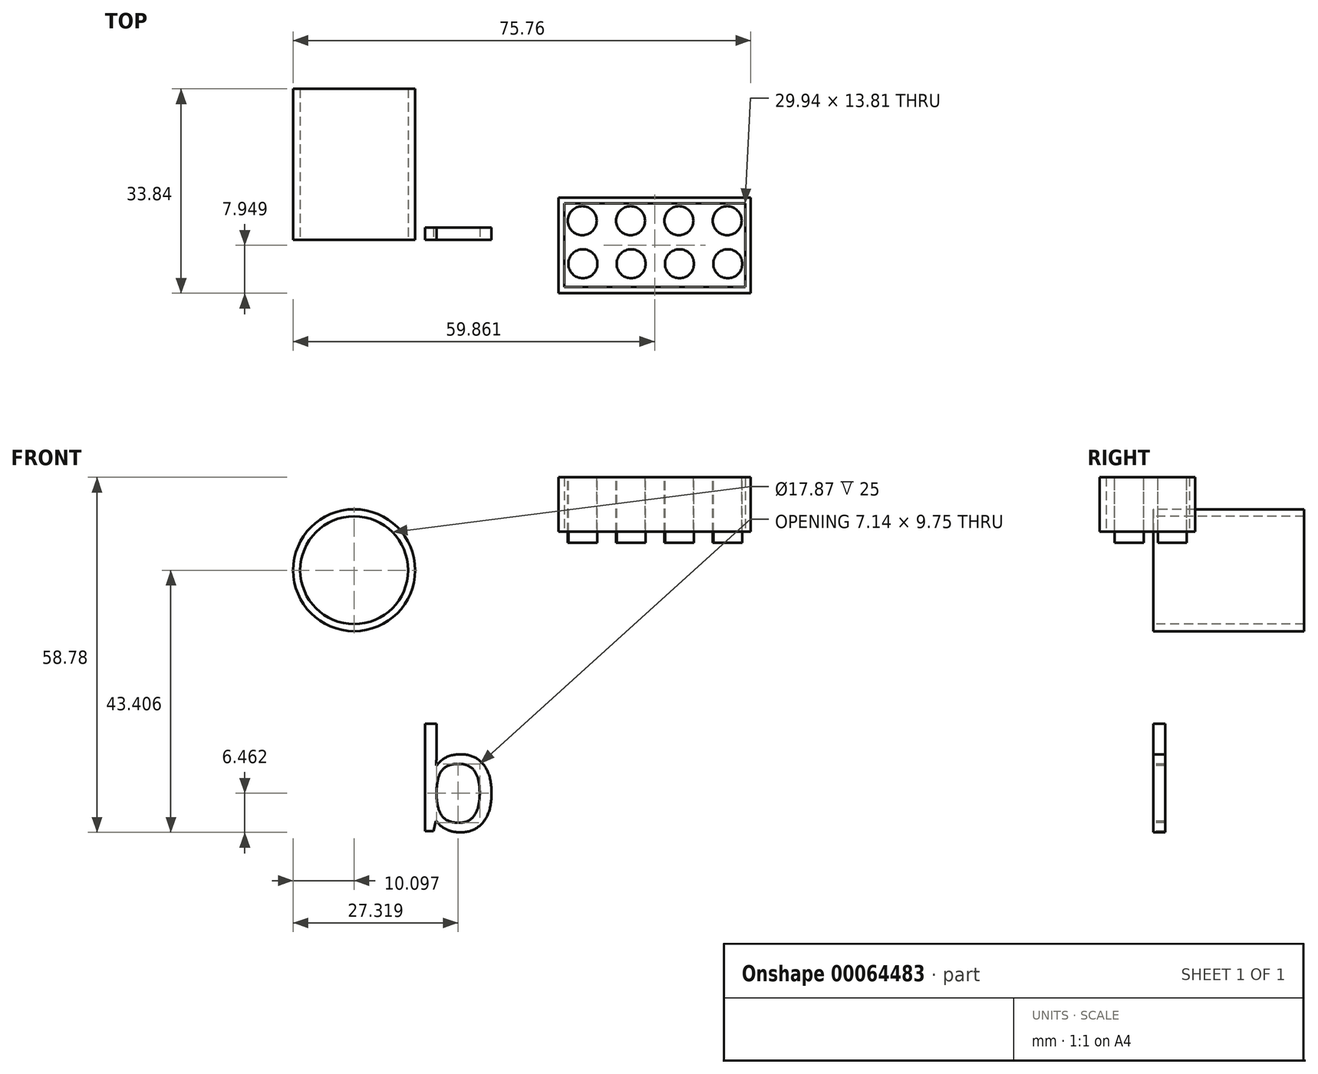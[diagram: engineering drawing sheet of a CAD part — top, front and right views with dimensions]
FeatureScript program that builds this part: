
annotation { "Feature Type Name" : "Feature", "Feature Type Description" : "" }
export const myFeature = defineFeature(function(context is Context, id is Id, definition is map)
    precondition{}
    {
        {
            var Q0;
            Q0=qCreatedBy(makeId("Top.planeOp"),FACE);
            var sketch = newSketch(context, id + "F0", { "sketchPlane" : qUnion([Q0])});
            skLineSegment(sketch, "E0.bottom", {"start": v(13.03, -8.84) * mm, "end": v(-18.77, -8.84) * mm});
            skLineSegment(sketch, "E0.top", {"start": v(13.03, 6.96) * mm, "end": v(-18.77, 6.96) * mm});
            skLineSegment(sketch, "E0.left", {"start": v(13.03, -8.84) * mm, "end": v(13.03, 6.96) * mm});
            skLineSegment(sketch, "E0.right", {"start": v(-18.77, -8.84) * mm, "end": v(-18.77, 6.96) * mm});
            skLineSegment(sketch, "E1.bottom", {"start": v(12.1, 6.02) * mm, "end": v(-17.84, 6.02) * mm});
            skLineSegment(sketch, "E1.top", {"start": v(12.1, -7.8) * mm, "end": v(-17.84, -7.8) * mm});
            skLineSegment(sketch, "E1.left", {"start": v(12.1, 6.02) * mm, "end": v(12.1, -7.8) * mm});
            skLineSegment(sketch, "E1.right", {"start": v(-17.84, 6.02) * mm, "end": v(-17.84, -7.8) * mm});
            skSolve(sketch);
        }
        {
            var Q0;
            Q0=makeQuery(id+"F0.imprint","IMPRINT",FACE,{"disambiguationData":[TD([[makeQuery(id+"F0.imprint","IMPRINT",EDGE,{"derivedFrom":sQuery(id+"F0.wireOp",EDGE,"E0.bottom")}),-1.0]])]});
            extrude(context, id + "F1", {"entities" : qUnion([Q0]), "depth" : 9 * mm});
        }
        {
            var Q0;
            Q0=makeQuery(id+"F1.opExtrude","CAP_FACE",FACE,{"disambiguationData":[OSD([sQuery(id+"F0.wireOp",EDGE,"E0.bottom"),sQuery(id+"F0.wireOp",EDGE,"E0.top"),sQuery(id+"F0.wireOp",EDGE,"E0.left"),sQuery(id+"F0.wireOp",EDGE,"E0.right")])],"isStart":false});
            var sketch = newSketch(context, id + "F2", { "sketchPlane" : qUnion([Q0])});
            skCircle(sketch, "E2", {"center": v(-14.87, 3.16) * mm, "radius": 2.4 * mm});
            skCircle(sketch, "E3.1.0.0", {"center": v(-6.87, 3.16) * mm, "radius": 2.4 * mm});
            skCircle(sketch, "E3.2.0.0", {"center": v(1.13, 3.16) * mm, "radius": 2.4 * mm});
            skCircle(sketch, "E3.3.0.0", {"center": v(9.13, 3.16) * mm, "radius": 2.4 * mm});
            skLineSegment(sketch, "E3.direction1", {"start": v(-14.87, 3.16) * mm, "end": v(-6.87, 3.16) * mm, "construction": true});
            skCircle(sketch, "E4.0.1.0", {"center": v(-14.76, -3.97) * mm, "radius": 2.4 * mm});
            skCircle(sketch, "E4.1.1.0", {"center": v(-6.76, -3.97) * mm, "radius": 2.4 * mm});
            skCircle(sketch, "E4.2.1.0", {"center": v(1.24, -3.97) * mm, "radius": 2.4 * mm});
            skCircle(sketch, "E4.3.1.0", {"center": v(9.24, -3.97) * mm, "radius": 2.4 * mm});
            skLineSegment(sketch, "E4.direction2", {"start": v(-14.87, 3.16) * mm, "end": v(-14.76, -3.97) * mm, "construction": true});
            skSolve(sketch);
        }
        {
            var Q0;
            Q0 = qSketchRegion(id + "F2", true);
            extrude(context, id + "F3", {"entities" : qUnion([Q0]), "operationType" : NewBodyOperationType.ADD, "oppositeDirection" : true, "depth" : 10.8 * mm});
        }
        {
            var Q0;
            Q0=qCreatedBy(makeId("Front.planeOp"),FACE);
            var sketch = newSketch(context, id + "F4", { "sketchPlane" : qUnion([Q0])});
            skCircle(sketch, "E5", {"center": v(-52.63, -6.37) * mm, "radius": 10.1 * mm});
            skCircle(sketch, "E6", {"center": v(-52.63, -6.37) * mm, "radius": 8.93 * mm});
            skText(sketch, "E7", { "text": "butt", "fontName": "OpenSans-Regular.ttf"});
            const initialGuessF4  = {"E7": [-0.04288, -0.04955, 1, 0, 0.0168]};
            skSetInitialGuess(sketch, initialGuessF4);
            skSolve(sketch);
        }
        {
            var Q0;
            Q0=makeQuery(id+"F4.imprint","IMPRINT",FACE,{"disambiguationData":[TD([[makeQuery(id+"F4.imprint","IMPRINT",EDGE,{"derivedFrom":sQuery(id+"F4.wireOp",EDGE,"E5")}),1.0]])]});
            extrude(context, id + "F5", {"entities" : qUnion([Q0]), "oppositeDirection" : true, "depth" : 25 * mm});
        }
        {
            var Q0;
            Q0=makeQuery(id+"F4.imprint","IMPRINT",FACE,{"disambiguationData":[TD([[makeQuery(id+"F4.imprint","IMPRINT",EDGE,{"derivedFrom":sQuery(id+"F4.wireOp",EDGE,"E7.sketch_text.stroke-0")}),-1.0]])]});
            extrude(context, id + "F6", {"entities" : qUnion([Q0]), "oppositeDirection" : true, "depth" : 2 * mm});
        }
    });
